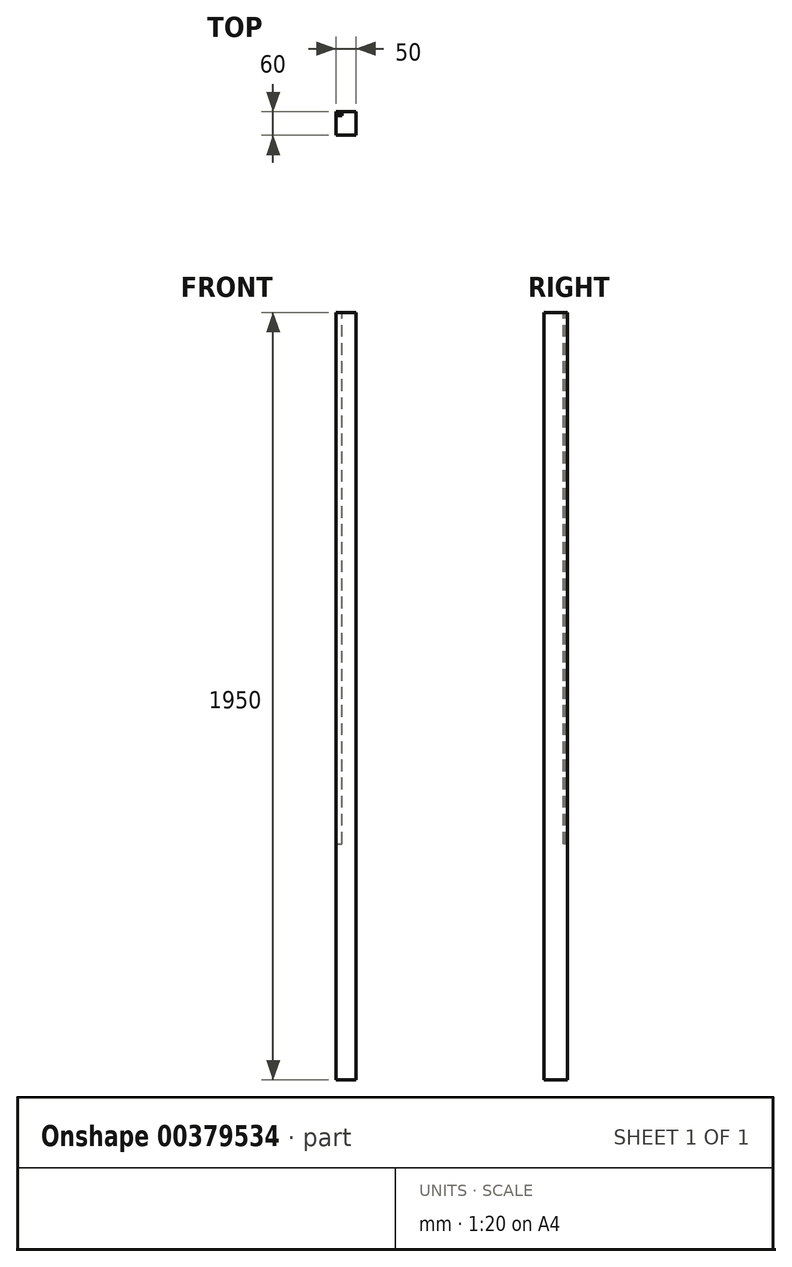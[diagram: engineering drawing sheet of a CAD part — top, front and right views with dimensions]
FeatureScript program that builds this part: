
annotation { "Feature Type Name" : "Feature", "Feature Type Description" : "" }
export const myFeature = defineFeature(function(context is Context, id is Id, definition is map)
    precondition{}
    {
        {
            var Q0;
            Q0=qCreatedBy(makeId("Top.planeOp"),FACE);
            var sketch = newSketch(context, id + "F0", { "sketchPlane" : qUnion([Q0])});
            skLineSegment(sketch, "E0.bottom", {"start": v(-25, 30) * mm, "end": v(25, 30) * mm});
            skLineSegment(sketch, "E0.top", {"start": v(-25, -30) * mm, "end": v(25, -30) * mm});
            skLineSegment(sketch, "E0.left", {"start": v(-25, 30) * mm, "end": v(-25, -30) * mm});
            skLineSegment(sketch, "E0.right", {"start": v(25, 30) * mm, "end": v(25, -30) * mm});
            skPoint(sketch, "E0.middle", {"position": v(0, 0) * mm});
            skSolve(sketch);
        }
        {
            var Q0;
            Q0=makeQuery(id+"F0.imprint","IMPRINT",FACE,{"disambiguationData":[TD([[makeQuery(id+"F0.imprint","IMPRINT",EDGE,{"derivedFrom":sQuery(id+"F0.wireOp",EDGE,"E0.bottom")}),-1.0]])]});
            extrude(context, id + "F1", {"entities" : qUnion([Q0]), "depth" : (150 * 9 + 600) * mm});
        }
        {
            var Q0;
            Q0=makeQuery(id+"F1.opExtrude","CAP_FACE",FACE,{"disambiguationData":[OSD([sQuery(id+"F0.wireOp",EDGE,"E0.bottom"),sQuery(id+"F0.wireOp",EDGE,"E0.top"),sQuery(id+"F0.wireOp",EDGE,"E0.left"),sQuery(id+"F0.wireOp",EDGE,"E0.right")])],"isStart":false});
            var sketch = newSketch(context, id + "F2", { "sketchPlane" : qUnion([Q0])});
            skLineSegment(sketch, "E1", {"start": v(-25, 30) * mm, "end": v(0, 30) * mm, "construction": true});
            skLineSegment(sketch, "E2", {"start": v(0, 30) * mm, "end": v(0, 35.95) * mm, "construction": true});
            skLineSegment(sketch, "E3.MirrorCS", {"start": v(-10, 26) * mm, "end": v(-10, 24) * mm});
            skLineSegment(sketch, "E4.MirrorCS", {"start": v(-25, 26) * mm, "end": v(-10, 26) * mm});
            skLineSegment(sketch, "E5.MirrorCS", {"start": v(-25, 28) * mm, "end": v(-25, 26) * mm});
            skLineSegment(sketch, "E6.MirrorCS", {"start": v(-10, 28) * mm, "end": v(-25, 28) * mm});
            skLineSegment(sketch, "E7.MirrorCS", {"start": v(-10, 30) * mm, "end": v(-10, 28) * mm});
            skLineSegment(sketch, "E8.MirrorCS", {"start": v(-25, 30) * mm, "end": v(-10, 30) * mm});
            skLineSegment(sketch, "E9.MirrorCS", {"start": v(-10, 20) * mm, "end": v(-25, 20) * mm});
            skLineSegment(sketch, "E10.MirrorCS", {"start": v(-10, 22) * mm, "end": v(-10, 20) * mm});
            skLineSegment(sketch, "E11.MirrorCS", {"start": v(-25, 22) * mm, "end": v(-10, 22) * mm});
            skLineSegment(sketch, "E12.MirrorCS", {"start": v(-10, 24) * mm, "end": v(-25, 24) * mm});
            skLineSegment(sketch, "E13.MirrorCS", {"start": v(-25, 24) * mm, "end": v(-25, 22) * mm});
            skSolve(sketch);
        }
        {
            var Q0;
            {var subQ0=sQuery(id+"F2.wireOp",EDGE,"E6.MirrorCS");Q0=makeQuery(id+"F2.imprint","IMPRINT",FACE,{"disambiguationData":[TD([[makeQuery(id+"F2.imprint","IMPRINT",EDGE,{"derivedFrom":subQ0}),-1.0]])]});}
            var Q1;
            Q1=makeQuery(id+"F2.imprint","IMPRINT",FACE,{"disambiguationData":[TD([[makeQuery(id+"F2.imprint","IMPRINT",EDGE,{"derivedFrom":sQuery(id+"F2.wireOp",EDGE,"E3.MirrorCS")}),-1.0]])]});
            var Q2;
            {var subQ0=sQuery(id+"F2.wireOp",EDGE,"E9.MirrorCS");Q2=makeQuery(id+"F2.imprint","IMPRINT",FACE,{"disambiguationData":[TD([[makeQuery(id+"F2.imprint","IMPRINT",EDGE,{"derivedFrom":subQ0}),-1.0]])]});}
            extrude(context, id + "F3", {"entities" : qUnion([Q0, Q1, Q2]), "operationType" : NewBodyOperationType.REMOVE, "oppositeDirection" : true, "depth" : (150 * 9) * mm});
        }
    });
